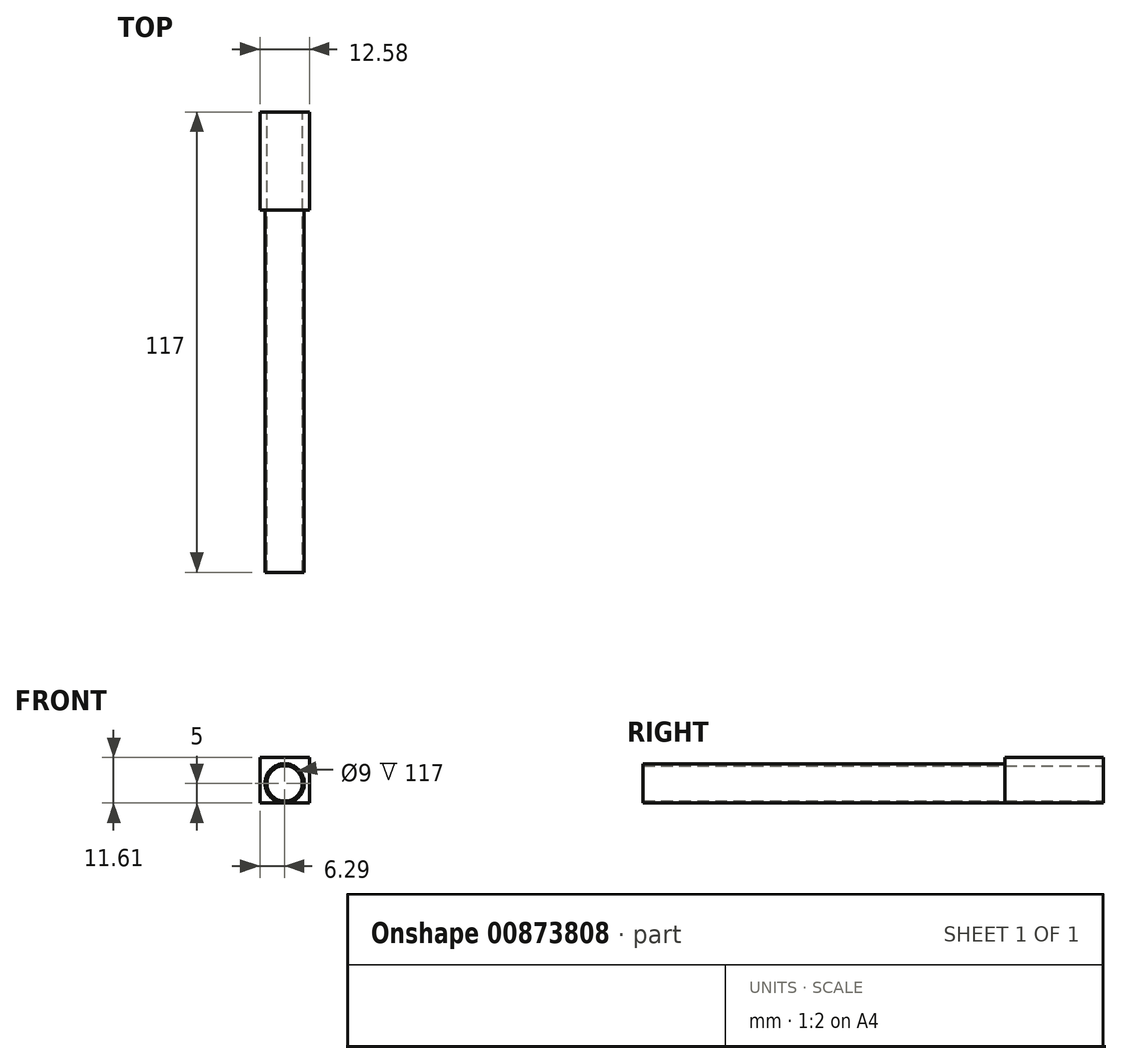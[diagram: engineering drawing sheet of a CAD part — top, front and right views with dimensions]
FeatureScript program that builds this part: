
annotation { "Feature Type Name" : "Feature", "Feature Type Description" : "" }
export const myFeature = defineFeature(function(context is Context, id is Id, definition is map)
    precondition{}
    {
        {
            var Q0;
            Q0=qCreatedBy(makeId("Front.planeOp"),FACE);
            var sketch = newSketch(context, id + "F0", { "sketchPlane" : qUnion([Q0])});
            skCircle(sketch, "E0", {"center": v(0, 0) * mm, "radius": 4.5 * mm});
            skCircle(sketch, "E1", {"center": v(0, 0) * mm, "radius": 5 * mm});
            skSolve(sketch);
        }
        {
            var Q0;
            Q0=makeQuery(id+"F0.imprint","IMPRINT",FACE,{"disambiguationData":[TD([[makeQuery(id+"F0.imprint","IMPRINT",EDGE,{"derivedFrom":sQuery(id+"F0.wireOp",EDGE,"E0")}),-1.0]])]});
            extrude(context, id + "F1", {"entities" : qUnion([Q0]), "depth" : 117 * mm, "offsetDistance" : 25 * mm});
        }
        {
            var Q0;
            Q0=qCreatedBy(makeId("Front.planeOp"),FACE);
            var sketch = newSketch(context, id + "F2", { "sketchPlane" : qUnion([Q0])});
            skCircle(sketch, "E2", {"center": v(0, 0) * mm, "radius": 4.5 * mm});
            skLineSegment(sketch, "E3", {"start": v(-6.29, 6.6) * mm, "end": v(6.3, 6.6) * mm});
            skLineSegment(sketch, "E4", {"start": v(6.3, 6.6) * mm, "end": v(6.3, -5) * mm});
            skLineSegment(sketch, "E5", {"start": v(6.3, -5) * mm, "end": v(-6.29, -5) * mm});
            skLineSegment(sketch, "E6", {"start": v(-6.29, -5) * mm, "end": v(-6.29, 6.6) * mm});
            skSolve(sketch);
        }
        {
            var Q0;
            Q0 = qSketchRegion(id + "F2", true);
            extrude(context, id + "F3", {"entities" : qUnion([Q0]), "operationType" : NewBodyOperationType.ADD, "depth" : 25 * mm, "offsetDistance" : 25 * mm});
        }
    });
